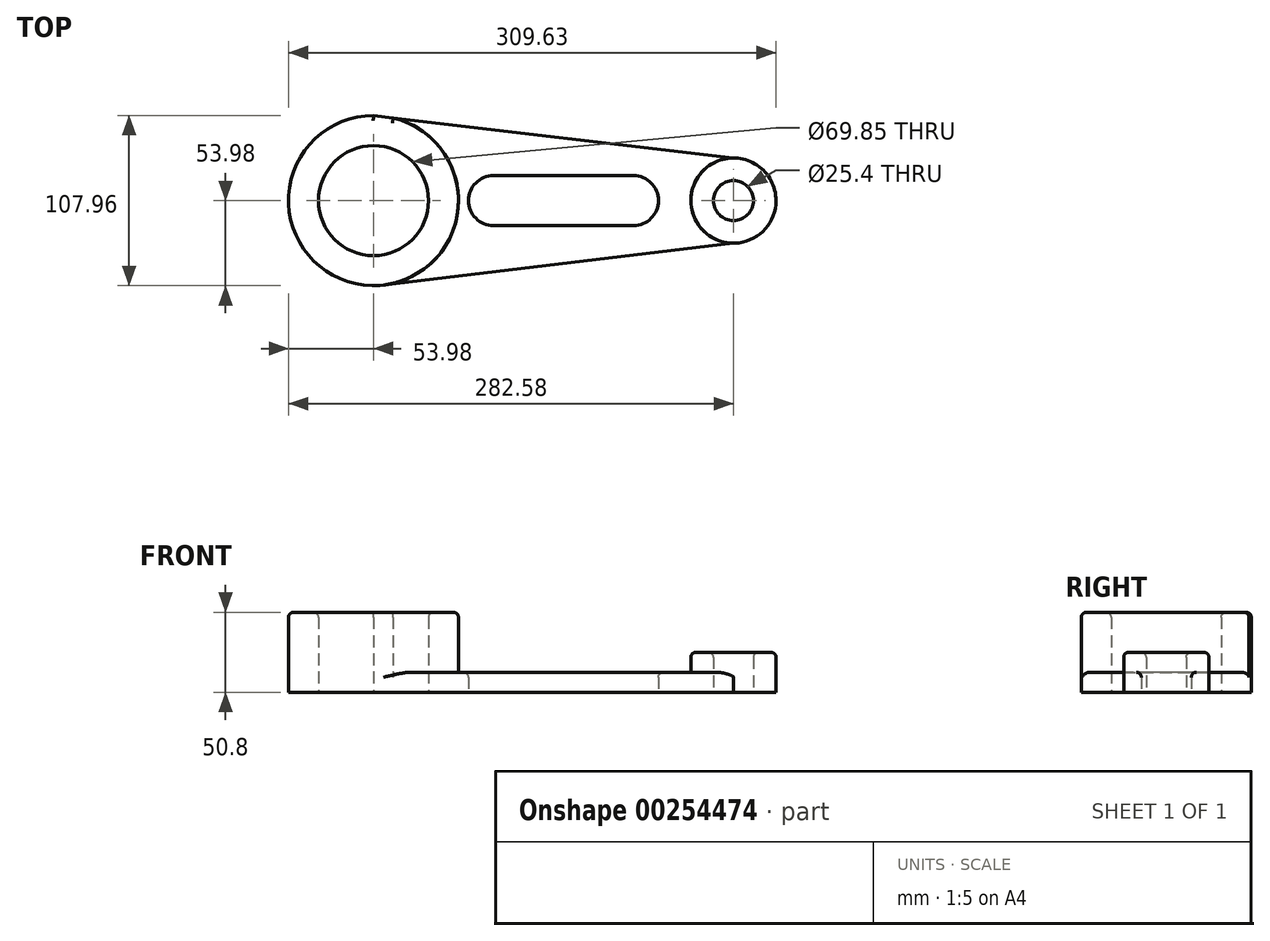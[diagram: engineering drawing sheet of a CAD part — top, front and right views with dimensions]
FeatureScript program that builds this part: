
annotation { "Feature Type Name" : "Feature", "Feature Type Description" : "" }
export const myFeature = defineFeature(function(context is Context, id is Id, definition is map)
    precondition{}
    {
        {
            var Q0;
            Q0=qCreatedBy(makeId("Top.planeOp"),FACE);
            var sketch = newSketch(context, id + "F0", { "sketchPlane" : qUnion([Q0])});
            skCircle(sketch, "E0", {"center": v(-76.2, 0) * mm, "radius": 34.93 * mm});
            skCircle(sketch, "E1", {"center": v(-76.2, 0) * mm, "radius": 53.98 * mm});
            skArc(sketch, "E2", {"start": v(0, 15.88) * mm, "mid": v(-15.88, 0) * mm, "end": v(0, -15.88) * mm});
            skArc(sketch, "E3", {"start": v(88.9, -15.88) * mm, "mid": v(104.78, 0) * mm, "end": v(88.9, 15.88) * mm});
            skLineSegment(sketch, "E4", {"start": v(0, 15.88) * mm, "end": v(88.9, 15.88) * mm});
            skLineSegment(sketch, "E5", {"start": v(0, -15.88) * mm, "end": v(88.9, -15.88) * mm});
            skCircle(sketch, "E6", {"center": v(152.4, 0) * mm, "radius": 12.7 * mm});
            skCircle(sketch, "E7", {"center": v(152.4, 0) * mm, "radius": 27.05 * mm});
            skLineSegment(sketch, "E8", {"start": v(-76.2, 53.97) * mm, "end": v(152.4, 27.05) * mm});
            skLineSegment(sketch, "E9", {"start": v(152.35, -27.05) * mm, "end": v(-76.2, -54.36) * mm});
            skSolve(sketch);
        }
        {
            var Q0;
            Q0=makeQuery(id+"F0.imprint","IMPRINT",FACE,{"disambiguationData":[TD([[makeQuery(id+"F0.imprint","IMPRINT",EDGE,{"derivedFrom":sQuery(id+"F0.wireOp",EDGE,"E0")}),-1.0]])]});
            extrude(context, id + "F1", {"entities" : qUnion([Q0]), "depth" : 50.8 * mm});
        }
        {
            var Q0;
            Q0=makeQuery(id+"F0.imprint","IMPRINT",FACE,{"disambiguationData":[TD([[makeQuery(id+"F0.imprint","IMPRINT",EDGE,{"derivedFrom":sQuery(id+"F0.wireOp",EDGE,"E2")}),-1.0]])]});
            extrude(context, id + "F2", {"entities" : qUnion([Q0]), "operationType" : NewBodyOperationType.ADD, "depth" : 12.7 * mm});
        }
        {
            var Q0;
            Q0=makeQuery(id+"F0.imprint","IMPRINT",FACE,{"disambiguationData":[TD([[makeQuery(id+"F0.imprint","IMPRINT",EDGE,{"derivedFrom":sQuery(id+"F0.wireOp",EDGE,"E6")}),-1.0]])]});
            extrude(context, id + "F3", {"entities" : qUnion([Q0]), "operationType" : NewBodyOperationType.ADD, "depth" : 25.4 * mm});
        }
        {
            var Q0;
            Q0=makeQuery(id+"F2.opExtrude","CAP_EDGE",EDGE,{"disambiguationData":[OSD([sQuery(id+"F0.wireOp",EDGE,"E8")])],"isStart":false});
            var Q1;
            Q1=makeQuery(id+"F2.opExtrude","CAP_EDGE",EDGE,{"disambiguationData":[OSD([sQuery(id+"F0.wireOp",EDGE,"E9")])],"isStart":false});
            var Q2;
            Q2=makeQuery(id+"F1.opExtrude","CAP_EDGE",EDGE,{"disambiguationData":[OSD([sQuery(id+"F0.wireOp",EDGE,"E1")])],"isStart":false});
            var Q3;
            Q3=makeQuery(id+"F2.opExtrude","CAP_EDGE",EDGE,{"disambiguationData":[OSD([sQuery(id+"F0.wireOp",EDGE,"E1")])],"isStart":false});
            var Q4;
            Q4=makeQuery(id+"F3.opExtrude","CAP_EDGE",EDGE,{"disambiguationData":[OSD([sQuery(id+"F0.wireOp",EDGE,"E7")])],"isStart":false});
            var Q5;
            Q5=makeQuery(id+"F2.opExtrude","CAP_EDGE",EDGE,{"disambiguationData":[OSD([sQuery(id+"F0.wireOp",EDGE,"E7")])],"isStart":false});
            var Q6;
            Q6=makeQuery(id+"F1.opExtrude","CAP_EDGE",EDGE,{"disambiguationData":[OSD([sQuery(id+"F0.wireOp",EDGE,"E8")])],"isStart":false});
            var Q7;
            Q7=makeQuery(id+"F1.opExtrude","CAP_EDGE",EDGE,{"disambiguationData":[OSD([sQuery(id+"F0.wireOp",EDGE,"E0")])],"isStart":false});
            var Q8;
            Q8=makeQuery(id+"F3.opExtrude","CAP_EDGE",EDGE,{"disambiguationData":[OSD([sQuery(id+"F0.wireOp",EDGE,"E6")])],"isStart":false});
            fillet(context, id + "F4", {"entities" : qUnion([Q0, Q1, Q2, Q3, Q4, Q5, Q6, Q7, Q8]), "radius" : 3.17 * mm, "tangentPropagation" : true, "allowEdgeOverflow" : false});
        }
        {
            var Q0;
            Q0=makeQuery(id+"F2.opExtrude","CAP_EDGE",EDGE,{"disambiguationData":[OSD([sQuery(id+"F0.wireOp",EDGE,"E4")])],"isStart":false});
            var Q1;
            Q1=makeQuery(id+"F2.opExtrude","CAP_EDGE",EDGE,{"disambiguationData":[OSD([sQuery(id+"F0.wireOp",EDGE,"E2")])],"isStart":false});
            var Q2;
            Q2=makeQuery(id+"F2.opExtrude","CAP_EDGE",EDGE,{"disambiguationData":[OSD([sQuery(id+"F0.wireOp",EDGE,"E5")])],"isStart":false});
            var Q3;
            Q3=makeQuery(id+"F2.opExtrude","CAP_EDGE",EDGE,{"disambiguationData":[OSD([sQuery(id+"F0.wireOp",EDGE,"E3")])],"isStart":false});
            fillet(context, id + "F5", {"entities" : qUnion([Q0, Q1, Q2, Q3]), "radius" : 3.17 * mm, "tangentPropagation" : true, "allowEdgeOverflow" : false});
        }
    });
